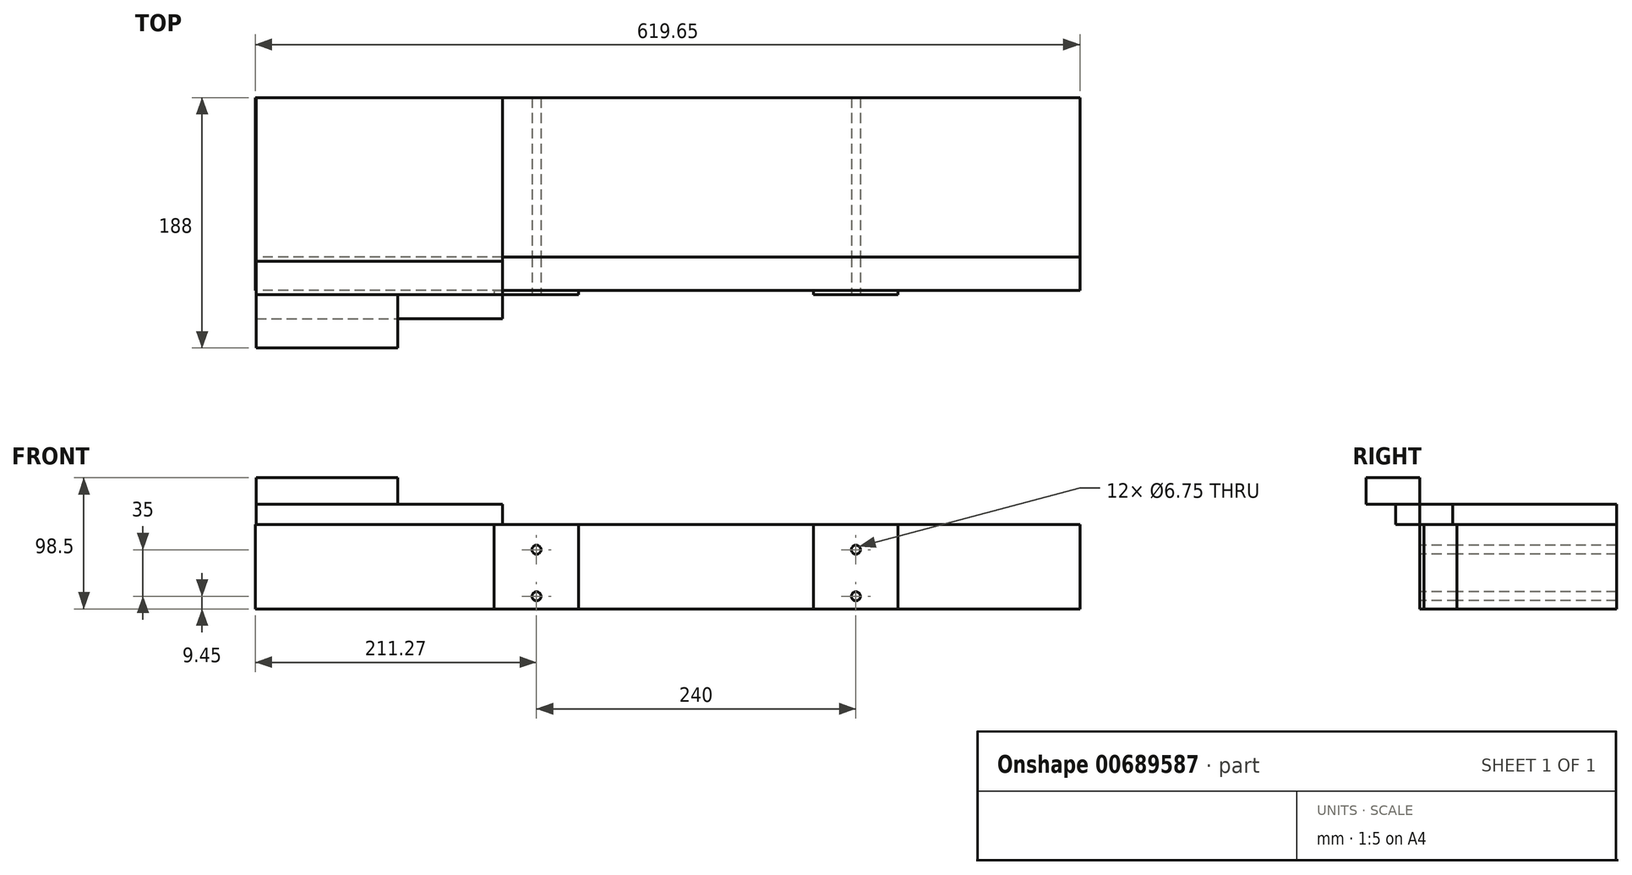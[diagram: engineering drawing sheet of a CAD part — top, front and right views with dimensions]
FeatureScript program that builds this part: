
annotation { "Feature Type Name" : "Feature", "Feature Type Description" : "" }
export const myFeature = defineFeature(function(context is Context, id is Id, definition is map)
    precondition{}
    {
        {
            var Q0;
            Q0=qCreatedBy(makeId("Front.planeOp"),FACE);
            var sketch = newSketch(context, id + "F0", { "sketchPlane" : qUnion([Q0])});
            skCircle(sketch, "E0", {"center": v(0, 0) * mm, "radius": 3.38 * mm});
            skCircle(sketch, "E1", {"center": v(240, 0) * mm, "radius": 3.38 * mm});
            skCircle(sketch, "E2.0.1.0", {"center": v(0, -35) * mm, "radius": 3.38 * mm});
            skCircle(sketch, "E2.0.1.1", {"center": v(240, -35) * mm, "radius": 3.38 * mm});
            skLineSegment(sketch, "E2.direction1", {"start": v(0, 0) * mm, "end": v(25, 0) * mm, "construction": true});
            skLineSegment(sketch, "E2.direction2", {"start": v(0, 0) * mm, "end": v(0, -35) * mm, "construction": true});
            skLineSegment(sketch, "E3.bottom", {"start": v(-210.68, 34.05) * mm, "end": v(-25.62, 34.05) * mm});
            skLineSegment(sketch, "E3.top", {"start": v(-210.68, 19.05) * mm, "end": v(-25.62, 19.05) * mm});
            skLineSegment(sketch, "E3.left", {"start": v(-210.68, 34.05) * mm, "end": v(-210.68, 19.05) * mm});
            skLineSegment(sketch, "E3.right", {"start": v(-25.62, 34.05) * mm, "end": v(-25.62, 19.05) * mm});
            skLineSegment(sketch, "E4.bottom", {"start": v(-104.37, 34.05) * mm, "end": v(-210.68, 34.05) * mm});
            skLineSegment(sketch, "E4.top", {"start": v(-104.37, 54.05) * mm, "end": v(-210.68, 54.05) * mm});
            skLineSegment(sketch, "E4.left", {"start": v(-104.37, 34.05) * mm, "end": v(-104.37, 54.05) * mm});
            skLineSegment(sketch, "E4.right", {"start": v(-210.68, 34.05) * mm, "end": v(-210.68, 54.05) * mm});
            skLineSegment(sketch, "E5.bottom", {"start": v(31.75, 19.05) * mm, "end": v(-31.75, 19.05) * mm});
            skLineSegment(sketch, "E5.top", {"start": v(31.75, -44.45) * mm, "end": v(-31.75, -44.45) * mm});
            skLineSegment(sketch, "E5.left", {"start": v(31.75, 19.05) * mm, "end": v(31.75, -44.45) * mm});
            skLineSegment(sketch, "E5.right", {"start": v(-31.75, 19.05) * mm, "end": v(-31.75, -44.45) * mm});
            skLineSegment(sketch, "E6.bottom", {"start": v(208.25, 19.05) * mm, "end": v(271.75, 19.05) * mm});
            skLineSegment(sketch, "E6.top", {"start": v(208.25, -44.45) * mm, "end": v(271.75, -44.45) * mm});
            skLineSegment(sketch, "E6.left", {"start": v(208.25, 19.05) * mm, "end": v(208.25, -44.45) * mm});
            skLineSegment(sketch, "E6.right", {"start": v(271.75, 19.05) * mm, "end": v(271.75, -44.45) * mm});
            skPoint(sketch, "E7", {"position": v(0, 19.05) * mm});
            skPoint(sketch, "E8", {"position": v(240, 19.05) * mm});
            skLineSegment(sketch, "E9.bottom", {"start": v(-31.75, 19.05) * mm, "end": v(-208.4, 19.05) * mm});
            skSolve(sketch);
        }
        {
            var Q0;
            {var subQ1=sQuery(id+"F0.wireOp",EDGE,"E3.bottom");Q0=makeQuery(id+"F0.imprint","IMPRINT",FACE,{"disambiguationData":[TD([[makeQuery(id+"F0.imprint","IMPRINT",EDGE,{"derivedFrom":subQ1}),-1.0]])]});}
            extrude(context, id + "F1", {"entities" : qUnion([Q0]), "depth" : 18 * mm, "offsetDistance" : 25 * mm});
        }
        {
            var Q0;
            Q0=makeQuery(id+"F0.imprint","IMPRINT",FACE,{"disambiguationData":[TD([[makeQuery(id+"F0.imprint","IMPRINT",EDGE,{"derivedFrom":sQuery(id+"F0.wireOp",EDGE,"E4.top")}),1.0]])]});
            extrude(context, id + "F2", {"entities" : qUnion([Q0]), "operationType" : NewBodyOperationType.ADD, "depth" : 40 * mm, "offsetDistance" : 25 * mm});
        }
        {
            var Q0;
            Q0=makeQuery(id+"F0.imprint","IMPRINT",FACE,{"disambiguationData":[TD([[makeQuery(id+"F0.imprint","IMPRINT",EDGE,{"derivedFrom":sQuery(id+"F0.wireOp",EDGE,"E0")}),-1.0]])]});
            var Q1;
            Q1=makeQuery(id+"F0.imprint","IMPRINT",FACE,{"disambiguationData":[TD([[makeQuery(id+"F0.imprint","IMPRINT",EDGE,{"derivedFrom":sQuery(id+"F0.wireOp",EDGE,"E1")}),-1.0]])]});
            extrude(context, id + "F3", {"entities" : qUnion([Q0, Q1]), "operationType" : NewBodyOperationType.ADD, "oppositeDirection" : true, "depth" : 3.17 * mm, "offsetDistance" : 25 * mm});
        }
        {
            var Q0;
            Q0=makeQuery(id+"F3.opExtrude","CAP_FACE",FACE,{"disambiguationData":[OSD([sQuery(id+"F0.wireOp",EDGE,"E1"),sQuery(id+"F0.wireOp",EDGE,"E2.0.1.1"),sQuery(id+"F0.wireOp",EDGE,"E6.bottom"),sQuery(id+"F0.wireOp",EDGE,"E6.top"),sQuery(id+"F0.wireOp",EDGE,"E6.left"),sQuery(id+"F0.wireOp",EDGE,"E6.right")])],"isStart":false});
            var sketch = newSketch(context, id + "F4", { "sketchPlane" : qUnion([Q0])});
            skLineSegment(sketch, "E10.bottom", {"start": v(-408.38, 19.05) * mm, "end": v(211.27, 19.05) * mm});
            skLineSegment(sketch, "E10.top", {"start": v(-408.38, -44.45) * mm, "end": v(211.27, -44.45) * mm});
            skLineSegment(sketch, "E10.left", {"start": v(-408.38, 19.05) * mm, "end": v(-408.38, -44.45) * mm});
            skLineSegment(sketch, "E10.right", {"start": v(211.27, 19.05) * mm, "end": v(211.27, -44.45) * mm});
            skSolve(sketch);
        }
        {
            var Q0;
            Q0=makeQuery(id+"F0.imprint","IMPRINT",FACE,{"disambiguationData":[TD([[makeQuery(id+"F0.imprint","IMPRINT",EDGE,{"derivedFrom":sQuery(id+"F0.wireOp",EDGE,"E3.bottom")}),-1.0]])]});
            var Q1;
            Q1=makeQuery(id+"F0.imprint","IMPRINT",FACE,{"disambiguationData":[TD([[makeQuery(id+"F0.imprint","IMPRINT",EDGE,{"derivedFrom":sQuery(id+"F0.wireOp",EDGE,"E4.bottom")}),-1.0]])]});
            var Q2;
            {var subQ2=sQuery(id+"F4.wireOp",EDGE,"E10.left");Q2=makeQuery(id+"F4.imprint","IMPRINT",FACE,{"disambiguationData":[TD([[makeQuery(id+"F4.imprint","IMPRINT",EDGE,{"derivedFrom":subQ2}),1.0]])]});}
            var Q3;
            Q3=makeQuery(id+"F4.imprint","IMPRINT",FACE,{"disambiguationData":[TD([[makeQuery(id+"F4.imprint","IMPRINT",EDGE,{"derivedFrom":makeQuery(id+"F3.opExtrude","CAP_EDGE",EDGE,{"disambiguationData":[OSD([sQuery(id+"F0.wireOp",EDGE,"E1")])],"isStart":false})}),1.0]])]});
            var Q4;
            {var subQ2=sQuery(id+"F4.wireOp",EDGE,"E10.right");Q4=makeQuery(id+"F4.imprint","IMPRINT",FACE,{"disambiguationData":[TD([[makeQuery(id+"F4.imprint","IMPRINT",EDGE,{"derivedFrom":subQ2}),-1.0]])]});}
            extrude(context, id + "F5", {"entities" : qUnion([Q0, Q1, Q2, Q3, Q4]), "oppositeDirection" : true, "depth" : 25 * mm, "offsetDistance" : 25 * mm});
        }
        {
            var Q0;
            Q0=makeQuery(id+"F0.imprint","IMPRINT",FACE,{"disambiguationData":[TD([[makeQuery(id+"F0.imprint","IMPRINT",EDGE,{"derivedFrom":sQuery(id+"F0.wireOp",EDGE,"E0")}),1.0]])]});
            var Q1;
            {var subQ0=sQuery(id+"F0.wireOp",EDGE,"E5.top");var subQ1=sQuery(id+"F0.wireOp",EDGE,"E2.0.1.0");var subQ2=makeQuery(id+"F0.imprint","INTERSECT",VERTEX,{"disambiguationData":[OD(0.0)],"derivedFrom":[subQ1,subQ0]});Q1=makeQuery(id+"F0.imprint","IMPRINT",FACE,{"disambiguationData":[TD([[makeQuery(id+"F0.imprint","IMPRINT",EDGE,{"disambiguationData":[TD([[subQ2,-1.0]])],"derivedFrom":subQ1}),1.0]])]});}
            var Q2;
            Q2=makeQuery(id+"F0.imprint","IMPRINT",FACE,{"disambiguationData":[TD([[makeQuery(id+"F0.imprint","IMPRINT",EDGE,{"derivedFrom":sQuery(id+"F0.wireOp",EDGE,"E1")}),1.0]])]});
            var Q3;
            {var subQ0=sQuery(id+"F0.wireOp",EDGE,"E6.top");var subQ1=sQuery(id+"F0.wireOp",EDGE,"E2.0.1.1");var subQ2=makeQuery(id+"F0.imprint","INTERSECT",VERTEX,{"disambiguationData":[OD(0.0)],"derivedFrom":[subQ1,subQ0]});Q3=makeQuery(id+"F0.imprint","IMPRINT",FACE,{"disambiguationData":[TD([[makeQuery(id+"F0.imprint","IMPRINT",EDGE,{"disambiguationData":[TD([[subQ2,1.0]])],"derivedFrom":subQ1}),1.0]])]});}
            extrude(context, id + "F6", {"entities" : qUnion([Q0, Q1, Q2, Q3]), "operationType" : NewBodyOperationType.REMOVE, "endBound" : BoundingType.THROUGH_ALL, "oppositeDirection" : true, "depth" : 25 * mm, "offsetDistance" : 25 * mm});
        }
        {
            var Q0;
            Q0=makeQuery(id+"F5.opExtrude","CAP_FACE",FACE,{"disambiguationData":[OSD([sQuery(id+"F0.wireOp",EDGE,"E3.bottom"),sQuery(id+"F0.wireOp",EDGE,"E3.top"),sQuery(id+"F0.wireOp",EDGE,"E3.left"),sQuery(id+"F0.wireOp",EDGE,"E3.right"),sQuery(id+"F0.wireOp",EDGE,"E4.top"),sQuery(id+"F0.wireOp",EDGE,"E4.left"),sQuery(id+"F0.wireOp",EDGE,"E4.right"),sQuery(id+"F0.wireOp",EDGE,"E5.bottom"),sQuery(id+"F0.wireOp",EDGE,"E9.bottom")])],"isStart":false});
            extrude(context, id + "F7", {"entities" : qUnion([Q0]), "depth" : 123 * mm, "offsetDistance" : 25 * mm});
        }
        {
            var Q0;
            Q0=makeQuery(id+"F5.opExtrude","CAP_FACE",FACE,{"disambiguationData":[OSD([sQuery(id+"F0.wireOp",EDGE,"E1"),sQuery(id+"F0.wireOp",EDGE,"E2.0.1.1"),sQuery(id+"F4.wireOp",EDGE,"E10.bottom"),sQuery(id+"F4.wireOp",EDGE,"E10.top"),sQuery(id+"F4.wireOp",EDGE,"E10.left"),sQuery(id+"F4.wireOp",EDGE,"E10.right")])],"isStart":false});
            var Q1;
            Q1=makeQuery(id+"F7.opExtrude","CAP_VERTEX",VERTEX,{"disambiguationData":[OSD([sQuery(id+"F0.wireOp",EDGE,"E3.right"),sQuery(id+"F0.wireOp",EDGE,"E5.bottom")])],"isStart":false});
            extrude(context, id + "F8", {"entities" : qUnion([Q0]), "endBound" : BoundingType.UP_TO_VERTEX, "depth" : 25 * mm, "endBoundEntityVertex" : qUnion([Q1]), "offsetDistance" : 25 * mm});
        }
    });
